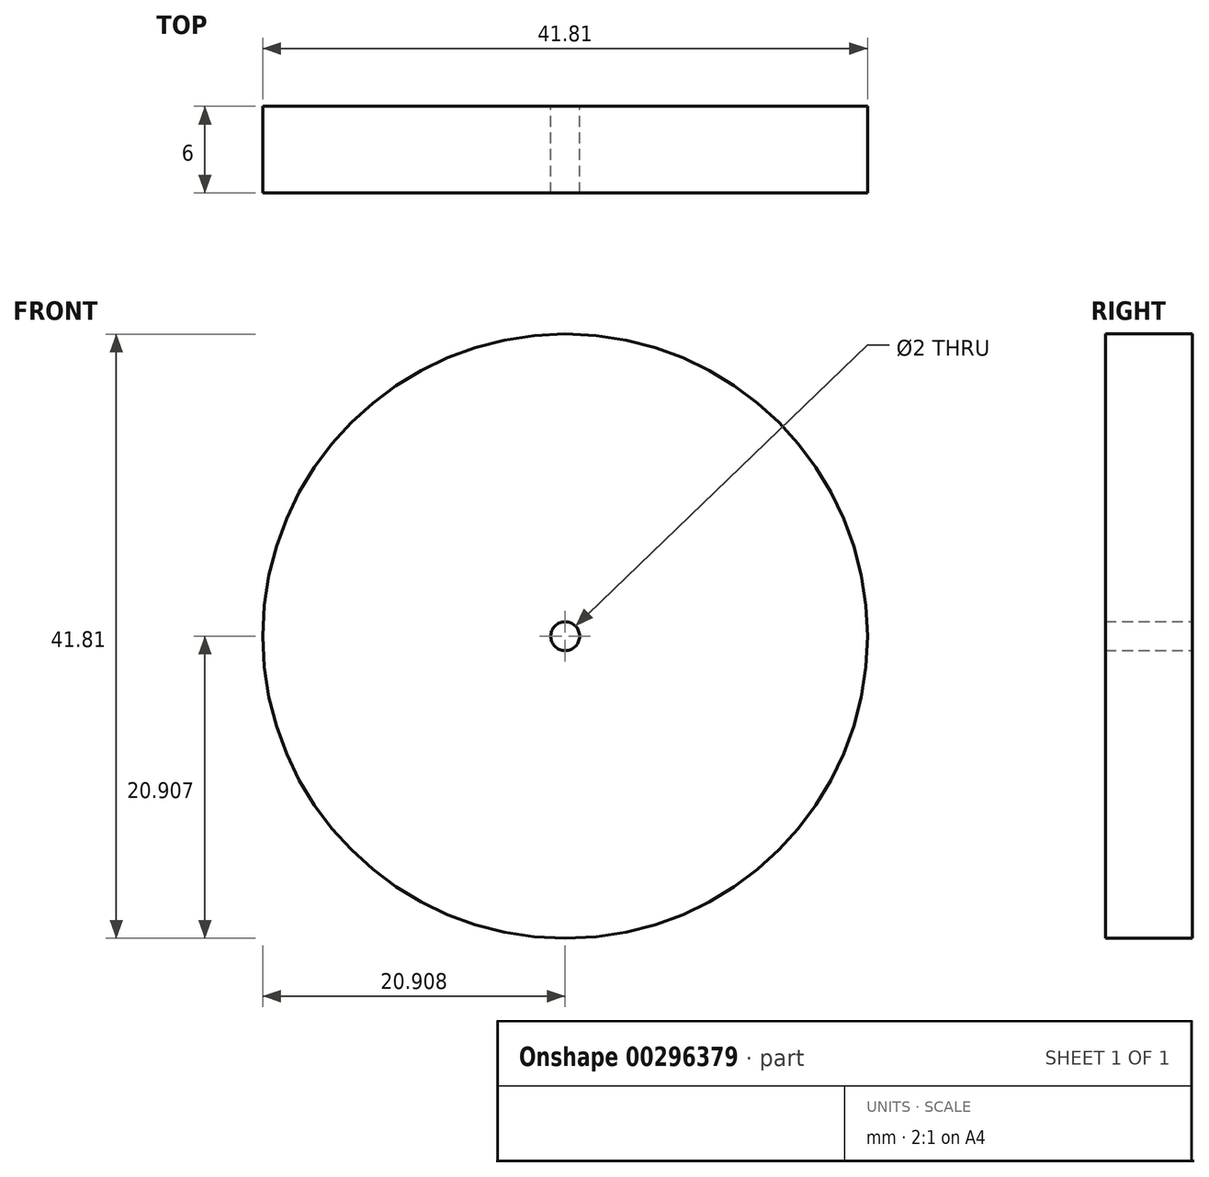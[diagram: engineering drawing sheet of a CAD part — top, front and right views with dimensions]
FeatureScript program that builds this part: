
annotation { "Feature Type Name" : "Feature", "Feature Type Description" : "" }
export const myFeature = defineFeature(function(context is Context, id is Id, definition is map)
    precondition{}
    {
        {
            var Q0;
            Q0=qCreatedBy(makeId("Front.planeOp"),FACE);
            var sketch = newSketch(context, id + "F0", { "sketchPlane" : qUnion([Q0])});
            skLineSegment(sketch, "E0", {"start": v(-315.7, 26.7) * mm, "end": v(-315.7, 74.5) * mm});
            skLineSegment(sketch, "E1", {"start": v(284.3, -98.96) * mm, "end": v(284.3, -134.36) * mm});
            skCircle(sketch, "E2", {"center": v(224.75, -213.44) * mm, "radius": 20.9 * mm});
            skCircle(sketch, "E3", {"center": v(224.75, -213.44) * mm, "radius": 1 * mm});
            skSolve(sketch);
        }
        {
            var Q0;
            Q0=makeQuery(id+"F0.imprint","IMPRINT",FACE,{"disambiguationData":[TD([[makeQuery(id+"F0.imprint","IMPRINT",EDGE,{"derivedFrom":sQuery(id+"F0.wireOp",EDGE,"E2")}),1.0]])]});
            extrude(context, id + "F1", {"entities" : qUnion([Q0]), "depth" : 6 * mm});
        }
    });
